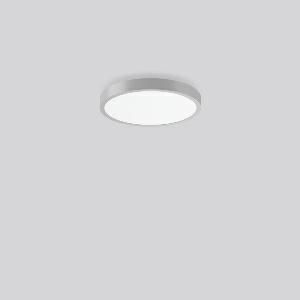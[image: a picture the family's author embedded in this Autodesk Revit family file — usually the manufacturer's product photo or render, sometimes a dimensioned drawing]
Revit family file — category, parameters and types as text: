
# Revit family: triona_round_a_312420_004_730_03c3
name_source: partatom
category: Lighting Fixtures
units: mm (PartAtom-declared; Revit-internal decimal feet)

## family parameters
Cut with Voids When Loaded = No
Host = Face
Light Source = No
Part Type = Normal
Room Calculation Point = No
Round Connector Dimension = Use Diameter
Shared = No

## types (1)
- TRIONA round A (1 x LED Modul 830, 5850 lm, 3000)
    Apparent Load = 64 VA
    CIE Flux Codes = 49 80 96 82 100
    Color Rendering = 80
    Color Temperature = 3000
    Default Elevation = 1800 mm
    Description = Series: TRIONA round
Decorative round LED surface-mounted luminaire. Flat, seamless frame: aluminium extrusion profile, powder coated. Cover made of sheet steel, powder-coated. Direct light emission through a diffuser plastic opal. Indirect light emission through a flush diffuser made of satin-finish plastic. Lightguide and diffuser made of non-yellowing plastic (PMMA). Lateral light emission (RZB SIDELITE technology) for above-average homogeneous light distribution. Direct 70%, indirect 30% light emission. Suitable for Ceiling mounting, Wall (surface). Tool-free mounting via bayonet connection. Electronic ballast included. Very easy installation thanks to Plug+Play connection. With Casambi smart+free Bluetooth control for wireless network and operation using Android / iOS devices, free app available for download. 
Colour: silver, matt (approx. RAL 9006)
Diameter: 461 mm
Height: 88 mm
Lamp: LED
Socket: without socket
Colour temperature: 3000K
Colour rendering index (CRI): 80
System power: 64 W
Rated luminous flux: 5850 lm
Luminous efficiency: 91 lm/W
Control gear: Dimmable Bluetooth converter
Protection class: I
Type of protection: IP 20
    Height = 88 mm
    Lamp = 1 x LED Modul 830
    Lamp Light Flux = 5850 lm
    Lamp count = 1
    Length = 461 mm
    Lifetime = 50000 h
    Luminous efficacy = 91 lm/W
    Manufacturer = RZB
    ModVariant = No
    Model = 312420.004.730
    Mounting Place = Ceiling
    Mounting Type = Surface mounted
    Number of Poles = 1
    OnlyDefault = Yes
    Power Factor = 1
    Product Name = TRIONA round A
    Product group = Surface mounted modular luminaires
    ProductGroupID = 306
    Protection Class = Protection class I
    Protection Degree = IP 20
    RLX_Detail_Level = 1
    RLX_Emergency_Light_Flux = 0 lm
    RLX_Emergency_Type = 0
    RLX_Emergency_Type_DB = No
    RlxData = <blob elided: 36985 chars, md5=6223a406>
    Socket = socket
    Standby Power = 0 W
    System Light Flux = 5850 lm
    System Power = 64 W
    Type Comments = Product without accessories
    Type Image = 312420.004.jpg
    URL = http://relux.com
    VarID = ---
    Voltage = 230 V
    Voltage Range = 220-240 V
    Weight = 0.00 kg
    Width = 0 mm  [stored 0 ft]

note: [stored X ft] marks values corroborated as IEEE doubles in the binary element streams (Revit-internal decimal feet)

## geometry (parser evidence)
native form markers: Blend x4, Sweep x12
no freeform markers — native parametric forms only
